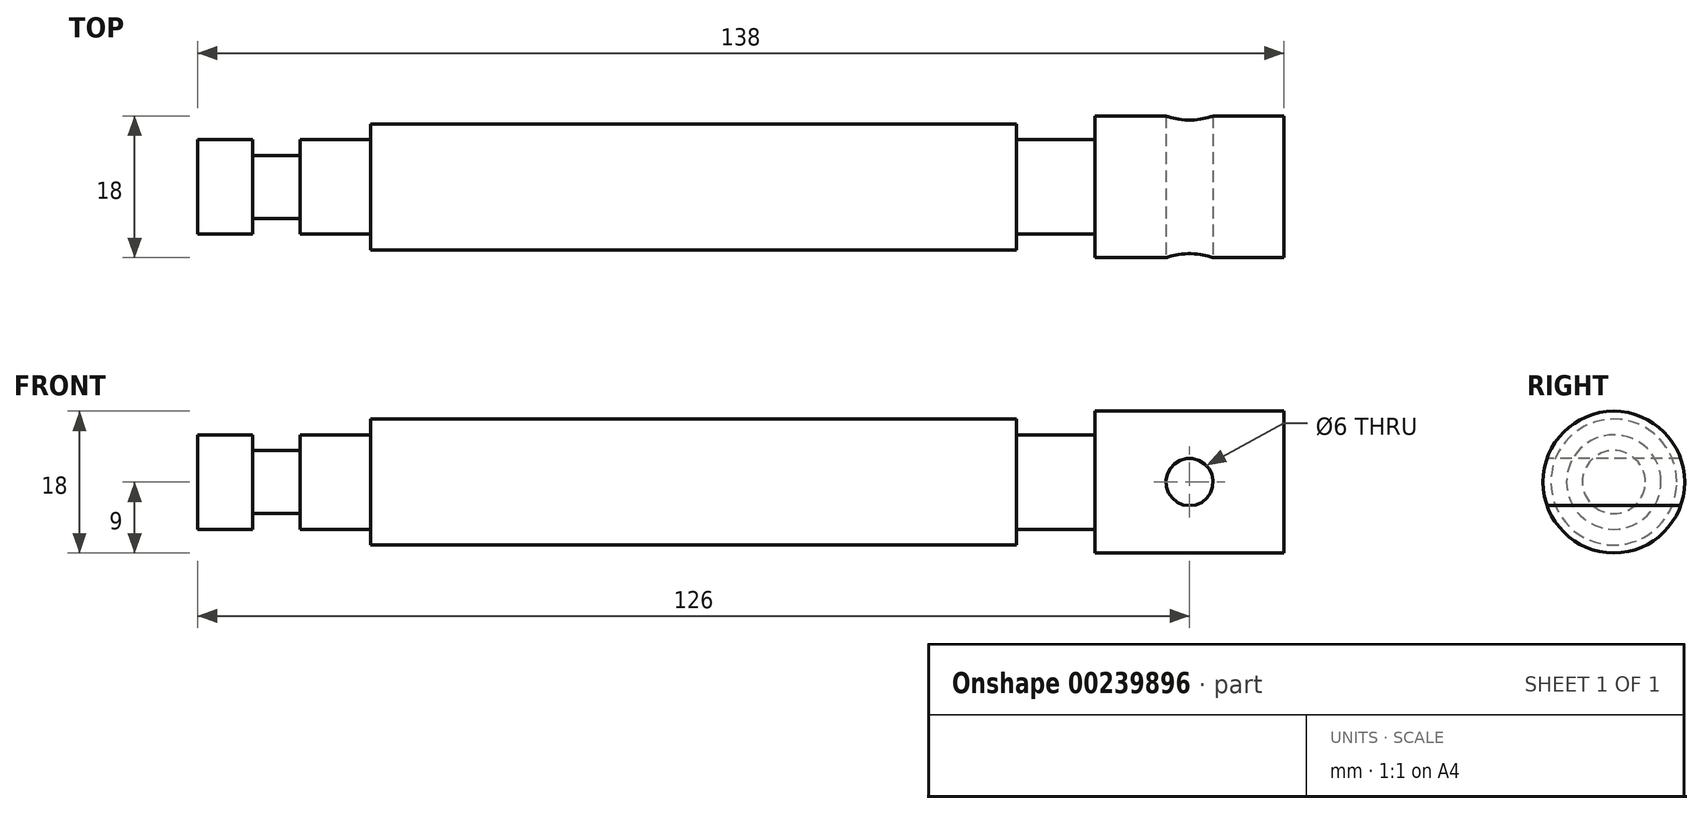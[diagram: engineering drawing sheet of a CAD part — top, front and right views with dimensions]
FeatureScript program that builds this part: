
annotation { "Feature Type Name" : "Feature", "Feature Type Description" : "" }
export const myFeature = defineFeature(function(context is Context, id is Id, definition is map)
    precondition{}
    {
        {
            var Q0;
            Q0=qCreatedBy(makeId("Front.planeOp"),FACE);
            var sketch = newSketch(context, id + "F0", { "sketchPlane" : qUnion([Q0])});
            skLineSegment(sketch, "E0", {"start": v(-69, 0) * mm, "end": v(-69, 6) * mm});
            skLineSegment(sketch, "E1", {"start": v(-69, 6) * mm, "end": v(-62, 6) * mm});
            skLineSegment(sketch, "E2", {"start": v(-62, 6) * mm, "end": v(-62, 4) * mm});
            skLineSegment(sketch, "E3", {"start": v(-62, 4) * mm, "end": v(-56, 4) * mm});
            skLineSegment(sketch, "E4", {"start": v(-56, 4) * mm, "end": v(-56, 6) * mm});
            skLineSegment(sketch, "E5", {"start": v(-56, 6) * mm, "end": v(-47, 6) * mm});
            skLineSegment(sketch, "E6", {"start": v(-47, 6) * mm, "end": v(-47, 8) * mm});
            skLineSegment(sketch, "E7", {"start": v(-47, 8) * mm, "end": v(35, 8) * mm});
            skLineSegment(sketch, "E8", {"start": v(35, 8) * mm, "end": v(35, 6) * mm});
            skLineSegment(sketch, "E9", {"start": v(35, 6) * mm, "end": v(45, 6) * mm});
            skLineSegment(sketch, "E10", {"start": v(45, 6) * mm, "end": v(45, 9) * mm});
            skLineSegment(sketch, "E11", {"start": v(45, 9) * mm, "end": v(69, 9) * mm});
            skLineSegment(sketch, "E12", {"start": v(69, 9) * mm, "end": v(69, 0) * mm});
            skLineSegment(sketch, "E13", {"start": v(69, 0) * mm, "end": v(-69, 0) * mm});
            skCircle(sketch, "E14", {"center": v(57, 0) * mm, "radius": 3 * mm});
            skSolve(sketch);
        }
        {
            var Q0;
            Q0=makeQuery(id+"F0.imprint","IMPRINT",FACE,{"disambiguationData":[TD([[makeQuery(id+"F0.imprint","IMPRINT",EDGE,{"derivedFrom":sQuery(id+"F0.wireOp",EDGE,"E0")}),-1.0]])]});
            var Q1;
            {var subQ0=sQuery(id+"F0.wireOp",EDGE,"E14");var subQ1=sQuery(id+"F0.wireOp",EDGE,"E13");var subQ2=makeQuery(id+"F0.imprint","INTERSECT",VERTEX,{"disambiguationData":[OD(0.0)],"derivedFrom":[subQ1,subQ0]});Q1=makeQuery(id+"F0.imprint","IMPRINT",FACE,{"disambiguationData":[TD([[makeQuery(id+"F0.imprint","IMPRINT",EDGE,{"disambiguationData":[TD([[subQ2,-1.0]])],"derivedFrom":subQ1}),-1.0]])]});}
            var Q2;
            Q2=sQuery(id+"F0.wireOp",EDGE,"E13");
            revolve(context, id + "F1", {"entities" : qUnion([Q0, Q1]), "axis" : qUnion([Q2]), "revolveType" : RevolveType.FULL});
        }
        {
            var Q0;
            {var subQ0=sQuery(id+"F0.wireOp",EDGE,"E14");var subQ1=sQuery(id+"F0.wireOp",EDGE,"E13");var subQ2=makeQuery(id+"F0.imprint","INTERSECT",VERTEX,{"disambiguationData":[OD(0.0)],"derivedFrom":[subQ1,subQ0]});Q0=makeQuery(id+"F0.imprint","IMPRINT",FACE,{"disambiguationData":[TD([[makeQuery(id+"F0.imprint","IMPRINT",EDGE,{"disambiguationData":[TD([[subQ2,-1.0]])],"derivedFrom":subQ1}),1.0]])]});}
            var Q1;
            {var subQ0=sQuery(id+"F0.wireOp",EDGE,"E14");var subQ1=sQuery(id+"F0.wireOp",EDGE,"E13");var subQ2=makeQuery(id+"F0.imprint","INTERSECT",VERTEX,{"disambiguationData":[OD(0.0)],"derivedFrom":[subQ1,subQ0]});Q1=makeQuery(id+"F0.imprint","IMPRINT",FACE,{"disambiguationData":[TD([[makeQuery(id+"F0.imprint","IMPRINT",EDGE,{"disambiguationData":[TD([[subQ2,-1.0]])],"derivedFrom":subQ1}),-1.0]])]});}
            extrude(context, id + "F2", {"entities" : qUnion([Q0, Q1]), "operationType" : NewBodyOperationType.REMOVE, "endBound" : BoundingType.SYMMETRIC, "oppositeDirection" : true, "depth" : 25 * mm});
        }
    });
